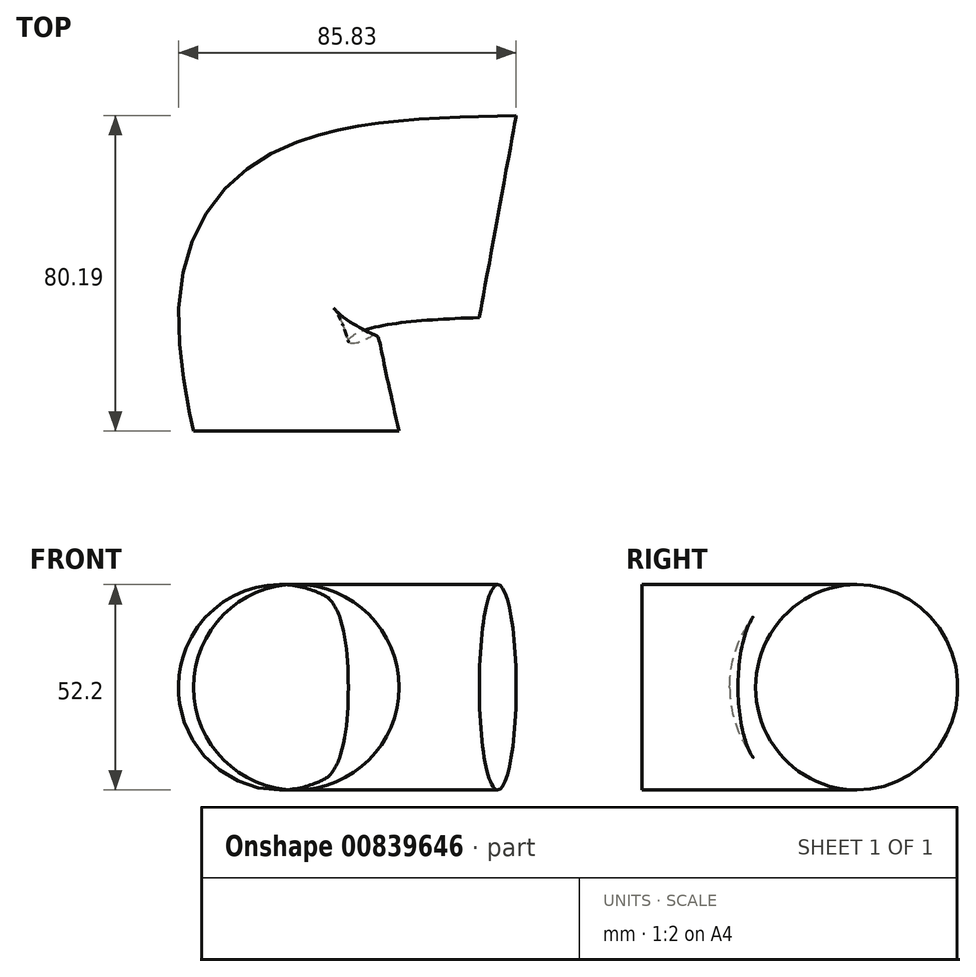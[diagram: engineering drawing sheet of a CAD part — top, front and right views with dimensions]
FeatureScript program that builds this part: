
annotation { "Feature Type Name" : "Feature", "Feature Type Description" : "" }
export const myFeature = defineFeature(function(context is Context, id is Id, definition is map)
    precondition{}
    {
        {
            var Q0;
            Q0=qCreatedBy(makeId("Front.planeOp"),FACE);
            var sketch = newSketch(context, id + "F0", { "sketchPlane" : qUnion([Q0])});
            skCircle(sketch, "E0", {"center": v(0, 0) * mm, "radius": 26.1 * mm});
            skSolve(sketch);
        }
        {
            var Q0;
            Q0=qCreatedBy(makeId("Top.planeOp"),FACE);
            var sketch = newSketch(context, id + "F1", { "sketchPlane" : qUnion([Q0])});
            skFitSpline(sketch, "E1", {"points": [v(0, 0) * mm, v(0, 42.96) * mm, v(51.2, 54.51) * mm], "startDerivative": vector(-23.16, 106.7) * mm, "endDerivative": vector(123.13, 4.05) * mm});
            skSolve(sketch);
        }
        {
            var Q0;
            Q0=makeQuery(id+"F0.imprint","IMPRINT",FACE,{"disambiguationData":[TD([[makeQuery(id+"F0.imprint","IMPRINT",EDGE,{"derivedFrom":sQuery(id+"F0.wireOp",EDGE,"E0")}),1.0]])]});
            var Q1;
            Q1=sQuery(id+"F0.wireOp",EDGE,"E0");
            var Q2;
            Q2 = qBodyType(qCreatedBy(id + "F1" ,EDGE), BodyType.WIRE);
            sweep(context, id + "F2", {"bodyType" : ToolBodyType.SURFACE, "profiles" : qUnion([Q0]), "surfaceProfiles" : qUnion([Q1]), "path" : qUnion([Q2])});
        }
    });
